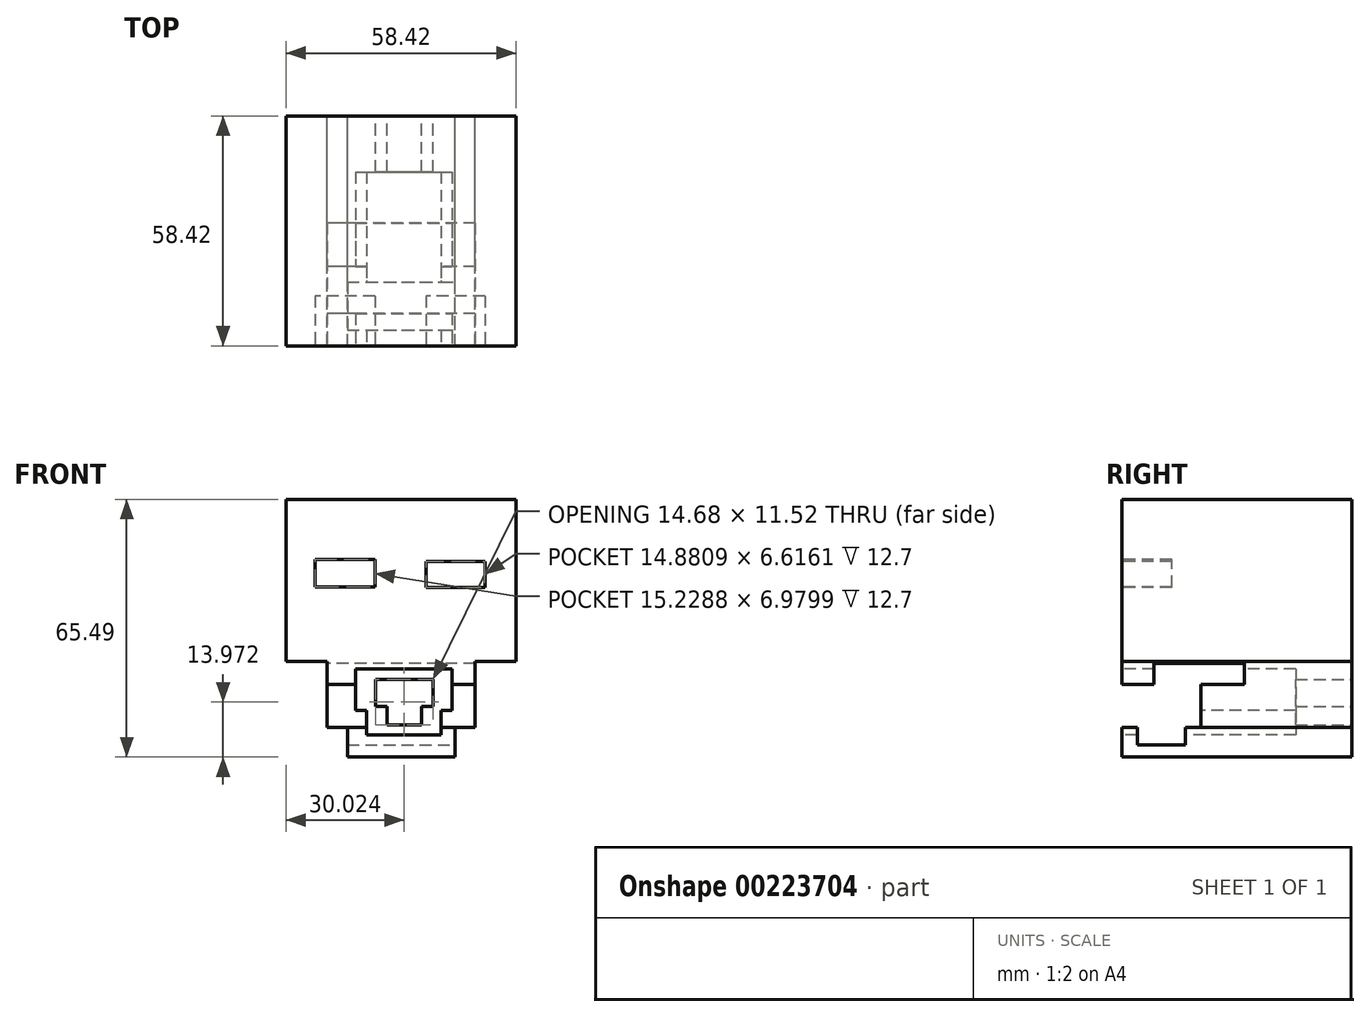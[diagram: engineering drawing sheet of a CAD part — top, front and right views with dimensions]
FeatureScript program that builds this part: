
annotation { "Feature Type Name" : "Feature", "Feature Type Description" : "" }
export const myFeature = defineFeature(function(context is Context, id is Id, definition is map)
    precondition{}
    {
        {
            var Q0;
            Q0=qCreatedBy(makeId("Front.planeOp"),FACE);
            var sketch = newSketch(context, id + "F0", { "sketchPlane" : qUnion([Q0])});
            skLineSegment(sketch, "E0.bottom", {"start": v(-29.2, 29.21) * mm, "end": v(29.21, 29.21) * mm});
            skLineSegment(sketch, "E0.left", {"start": v(-29.2, 29.21) * mm, "end": v(-29.21, -11.99) * mm});
            skLineSegment(sketch, "E0.right", {"start": v(29.21, 29.21) * mm, "end": v(29.2, -11.99) * mm});
            skPoint(sketch, "E0.middle", {"position": v(0, 0) * mm});
            skLineSegment(sketch, "E1", {"start": v(-29.21, -11.99) * mm, "end": v(-18.84, -11.99) * mm});
            skLineSegment(sketch, "E2", {"start": v(-18.84, -11.99) * mm, "end": v(-18.84, -28.7) * mm});
            skLineSegment(sketch, "E3.MirrorCS", {"start": v(18.84, -11.99) * mm, "end": v(18.84, -28.7) * mm});
            skLineSegment(sketch, "E4", {"start": v(-18.84, -28.7) * mm, "end": v(-13.65, -28.7) * mm});
            skLineSegment(sketch, "E5", {"start": v(18.84, -28.7) * mm, "end": v(13.74, -28.7) * mm});
            skLineSegment(sketch, "E6", {"start": v(-13.65, -28.7) * mm, "end": v(-13.65, -36.28) * mm});
            skLineSegment(sketch, "E7", {"start": v(13.74, -28.7) * mm, "end": v(13.74, -36.28) * mm});
            skLineSegment(sketch, "E8", {"start": v(-13.65, -36.28) * mm, "end": v(13.74, -36.28) * mm});
            skLineSegment(sketch, "E9.trimOffspring", {"start": v(18.84, -11.99) * mm, "end": v(29.2, -11.99) * mm});
            skSolve(sketch);
        }
        {
            var Q0;
            Q0 = qSketchRegion(id + "F0", true);
            extrude(context, id + "F1", {"entities" : qUnion([Q0]), "endBound" : BoundingType.SYMMETRIC, "depth" : 58.42 * mm});
        }
        {
            var Q0;
            Q0=makeQuery(id+"F1.opExtrude","CAP_FACE",FACE,{"disambiguationData":[OSD([sQuery(id+"F0.wireOp",EDGE,"E0.bottom"),sQuery(id+"F0.wireOp",EDGE,"E0.top"),sQuery(id+"F0.wireOp",EDGE,"E0.left"),sQuery(id+"F0.wireOp",EDGE,"E0.right")])],"isStart":false});
            var sketch = newSketch(context, id + "F2", { "sketchPlane" : qUnion([Q0])});
            skLineSegment(sketch, "E10.bottom", {"start": v(-6.65, 6.9) * mm, "end": v(-21.88, 6.9) * mm});
            skLineSegment(sketch, "E10.top", {"start": v(-6.65, 13.88) * mm, "end": v(-21.88, 13.88) * mm});
            skLineSegment(sketch, "E10.left", {"start": v(-6.65, 6.9) * mm, "end": v(-6.65, 13.88) * mm});
            skLineSegment(sketch, "E10.right", {"start": v(-21.88, 6.9) * mm, "end": v(-21.88, 13.88) * mm});
            skLineSegment(sketch, "E11.bottom", {"start": v(21.27, 6.85) * mm, "end": v(6.4, 6.85) * mm});
            skLineSegment(sketch, "E11.top", {"start": v(21.27, 13.46) * mm, "end": v(6.4, 13.46) * mm});
            skLineSegment(sketch, "E11.left", {"start": v(21.27, 6.85) * mm, "end": v(21.27, 13.46) * mm});
            skLineSegment(sketch, "E11.right", {"start": v(6.4, 6.85) * mm, "end": v(6.4, 13.46) * mm});
            skSolve(sketch);
        }
        {
            var Q0;
            Q0=makeQuery(id+"F2.imprint","IMPRINT",FACE,{"disambiguationData":[TD([[makeQuery(id+"F2.imprint","IMPRINT",EDGE,{"derivedFrom":sQuery(id+"F2.wireOp",EDGE,"89d0a196-2e3c-4021-a17d-25c8eb369dc5.bottom")}),-1.0]])]});
            var Q1;
            Q1=makeQuery(id+"F2.imprint","IMPRINT",FACE,{"disambiguationData":[TD([[makeQuery(id+"F2.imprint","IMPRINT",EDGE,{"derivedFrom":sQuery(id+"F2.wireOp",EDGE,"E10.bottom")}),-1.0]])]});
            var Q2;
            Q2=makeQuery(id+"F2.imprint","IMPRINT",FACE,{"disambiguationData":[TD([[makeQuery(id+"F2.imprint","IMPRINT",EDGE,{"derivedFrom":sQuery(id+"F2.wireOp",EDGE,"E11.bottom")}),-1.0]])]});
            extrude(context, id + "F3", {"entities" : qUnion([Q0, Q1, Q2]), "operationType" : NewBodyOperationType.REMOVE, "oppositeDirection" : true, "depth" : 12.7 * mm});
        }
        {
            var Q0;
            Q0=makeQuery(id+"F2.imprint","IMPRINT",FACE,{"disambiguationData":[TD([[makeQuery(id+"F2.imprint","IMPRINT",EDGE,{"derivedFrom":sQuery(id+"F2.wireOp",EDGE,"E10.bottom")}),1.0]])]});
            var sketch = newSketch(context, id + "F4", { "sketchPlane" : qUnion([Q0])});
            skLineSegment(sketch, "E12.top", {"start": v(-11.58, -24.48) * mm, "end": v(-8.78, -24.48) * mm});
            skLineSegment(sketch, "E12.left", {"start": v(-11.58, -13.84) * mm, "end": v(-11.58, -24.48) * mm});
            skLineSegment(sketch, "E12.right", {"start": v(12.97, -13.85) * mm, "end": v(12.97, -24.48) * mm});
            skLineSegment(sketch, "E13.top", {"start": v(-8.78, -30.6) * mm, "end": v(10.2, -30.6) * mm});
            skLineSegment(sketch, "E13.right", {"start": v(10.2, -24.48) * mm, "end": v(10.2, -30.6) * mm});
            skLineSegment(sketch, "E14.trimOffspring", {"start": v(10.2, -24.48) * mm, "end": v(12.97, -24.48) * mm});
            skLineSegment(sketch, "E15", {"start": v(-8.78, -24.48) * mm, "end": v(-8.78, -30.6) * mm});
            skLineSegment(sketch, "E16", {"start": v(-11.58, -13.84) * mm, "end": v(12.97, -13.85) * mm});
            skSolve(sketch);
        }
        {
            var Q0;
            Q0 = qSketchRegion(id + "F4", true);
            var Q1;
            Q1=makeQuery(id+"F1.opExtrude","CAP_FACE",FACE,{"disambiguationData":[OSD([sQuery(id+"F0.wireOp",EDGE,"E0.bottom"),sQuery(id+"F0.wireOp",EDGE,"E0.left"),sQuery(id+"F0.wireOp",EDGE,"E0.right"),sQuery(id+"F0.wireOp",EDGE,"E1"),sQuery(id+"F0.wireOp",EDGE,"E2"),sQuery(id+"F0.wireOp",EDGE,"E3.MirrorCS"),sQuery(id+"F0.wireOp",EDGE,"E4"),sQuery(id+"F0.wireOp",EDGE,"E5"),sQuery(id+"F0.wireOp",EDGE,"E6"),sQuery(id+"F0.wireOp",EDGE,"E7"),sQuery(id+"F0.wireOp",EDGE,"E8"),sQuery(id+"F0.wireOp",EDGE,"E9.trimOffspring")])],"isStart":true});
            extrude(context, id + "F5", {"entities" : qUnion([Q0]), "operationType" : NewBodyOperationType.REMOVE, "endBound" : BoundingType.UP_TO_SURFACE, "oppositeDirection" : true, "endBoundEntityFace" : qUnion([Q1]), "depth" : 25.4 * mm});
        }
        {
            var Q0;
            Q0=makeQuery(id+"F1.opExtrude","SWEPT_FACE",FACE,{"disambiguationData":[OSD([sQuery(id+"F0.wireOp",EDGE,"E2")])]});
            var sketch = newSketch(context, id + "F6", { "sketchPlane" : qUnion([Q0])});
            skLineSegment(sketch, "E17.bottom", {"start": v(-2, -12.45) * mm, "end": v(20.98, -12.45) * mm});
            skLineSegment(sketch, "E17.top", {"start": v(-2, -17.86) * mm, "end": v(9.04, -17.86) * mm});
            skLineSegment(sketch, "E17.left", {"start": v(-2, -12.45) * mm, "end": v(-2, -17.86) * mm});
            skLineSegment(sketch, "E17.right", {"start": v(20.98, -12.45) * mm, "end": v(20.98, -17.86) * mm});
            skLineSegment(sketch, "E18.bottom", {"start": v(20.98, -17.86) * mm, "end": v(29.31, -17.86) * mm});
            skLineSegment(sketch, "E18.top", {"start": v(9.04, -28.7) * mm, "end": v(29.31, -28.7) * mm});
            skLineSegment(sketch, "E18.left", {"start": v(9.04, -17.86) * mm, "end": v(9.04, -28.7) * mm});
            skLineSegment(sketch, "E18.right", {"start": v(29.31, -17.86) * mm, "end": v(29.31, -28.7) * mm});
            skSolve(sketch);
        }
        {
            var Q0;
            Q0 = qSketchRegion(id + "F6", true);
            var Q1;
            Q1=makeQuery(id+"F1.opExtrude","SWEPT_FACE",FACE,{"disambiguationData":[OSD([sQuery(id+"F0.wireOp",EDGE,"E3.MirrorCS")])]});
            extrude(context, id + "F7", {"entities" : qUnion([Q0]), "operationType" : NewBodyOperationType.REMOVE, "endBound" : BoundingType.UP_TO_SURFACE, "oppositeDirection" : true, "endBoundEntityFace" : qUnion([Q1]), "depth" : 25.4 * mm});
        }
        {
            var Q0;
            Q0=makeQuery(id+"F1.opExtrude","SWEPT_FACE",FACE,{"disambiguationData":[OSD([sQuery(id+"F0.wireOp",EDGE,"E7")])]});
            var sketch = newSketch(context, id + "F8", { "sketchPlane" : qUnion([Q0])});
            skLineSegment(sketch, "E19.bottom", {"start": v(-25.22, -33.19) * mm, "end": v(-13.05, -33.19) * mm});
            skLineSegment(sketch, "E19.top", {"start": v(-25.22, -28.7) * mm, "end": v(-13.05, -28.7) * mm});
            skLineSegment(sketch, "E19.left", {"start": v(-25.22, -33.19) * mm, "end": v(-25.22, -28.7) * mm});
            skLineSegment(sketch, "E19.right", {"start": v(-13.05, -33.19) * mm, "end": v(-13.05, -28.7) * mm});
            skSolve(sketch);
        }
        {
            var Q0;
            Q0 = qSketchRegion(id + "F8", true);
            var Q1;
            Q1=makeQuery(id+"F1.opExtrude","SWEPT_FACE",FACE,{"disambiguationData":[OSD([sQuery(id+"F0.wireOp",EDGE,"E6")])]});
            extrude(context, id + "F9", {"entities" : qUnion([Q0]), "operationType" : NewBodyOperationType.REMOVE, "endBound" : BoundingType.UP_TO_SURFACE, "oppositeDirection" : true, "endBoundEntityFace" : qUnion([Q1]), "depth" : 25.4 * mm});
        }
        {
            var Q0;
            Q0=makeQuery(id+"F1.opExtrude","CAP_FACE",FACE,{"disambiguationData":[OSD([sQuery(id+"F0.wireOp",EDGE,"E0.bottom"),sQuery(id+"F0.wireOp",EDGE,"E0.left"),sQuery(id+"F0.wireOp",EDGE,"E0.right"),sQuery(id+"F0.wireOp",EDGE,"E1"),sQuery(id+"F0.wireOp",EDGE,"E2"),sQuery(id+"F0.wireOp",EDGE,"E3.MirrorCS"),sQuery(id+"F0.wireOp",EDGE,"E4"),sQuery(id+"F0.wireOp",EDGE,"E5"),sQuery(id+"F0.wireOp",EDGE,"E6"),sQuery(id+"F0.wireOp",EDGE,"E7"),sQuery(id+"F0.wireOp",EDGE,"E8"),sQuery(id+"F0.wireOp",EDGE,"E9.trimOffspring")])],"isStart":true});
            var sketch = newSketch(context, id + "F10", { "sketchPlane" : qUnion([Q0])});
            skLineSegment(sketch, "E20.bottom", {"start": v(-15.34, -11.61) * mm, "end": v(12.82, -11.61) * mm});
            skLineSegment(sketch, "E20.top", {"start": v(-15.34, -26.3) * mm, "end": v(-12.97, -26.3) * mm});
            skLineSegment(sketch, "E20.left", {"start": v(-15.34, -11.61) * mm, "end": v(-15.34, -26.3) * mm});
            skLineSegment(sketch, "E20.right", {"start": v(12.82, -11.61) * mm, "end": v(12.82, -26.3) * mm});
            skLineSegment(sketch, "E21.trimOffspring", {"start": v(10.17, -26.3) * mm, "end": v(12.82, -26.3) * mm});
            skLineSegment(sketch, "E22", {"start": v(-12.97, -26.3) * mm, "end": v(-12.98, -31.88) * mm});
            skLineSegment(sketch, "E23", {"start": v(10.17, -26.3) * mm, "end": v(10.17, -31.88) * mm});
            skLineSegment(sketch, "E24", {"start": v(-12.98, -31.88) * mm, "end": v(10.17, -31.88) * mm});
            skSolve(sketch);
        }
        {
            var Q0;
            Q0 = qSketchRegion(id + "F10", true);
            extrude(context, id + "F11", {"entities" : qUnion([Q0]), "operationType" : NewBodyOperationType.ADD, "oppositeDirection" : true, "depth" : 14.22 * mm});
        }
        {
            var Q0;
            Q0=makeQuery(id+"F11.boolean.opBoolean","MERGE",FACE,{"derivedFrom":[makeQuery(id+"F1.opExtrude","CAP_FACE",FACE,{"disambiguationData":[OSD([sQuery(id+"F0.wireOp",EDGE,"E0.bottom"),sQuery(id+"F0.wireOp",EDGE,"E0.left"),sQuery(id+"F0.wireOp",EDGE,"E0.right"),sQuery(id+"F0.wireOp",EDGE,"E1"),sQuery(id+"F0.wireOp",EDGE,"E2"),sQuery(id+"F0.wireOp",EDGE,"E3.MirrorCS"),sQuery(id+"F0.wireOp",EDGE,"E4"),sQuery(id+"F0.wireOp",EDGE,"E5"),sQuery(id+"F0.wireOp",EDGE,"E6"),sQuery(id+"F0.wireOp",EDGE,"E7"),sQuery(id+"F0.wireOp",EDGE,"E8"),sQuery(id+"F0.wireOp",EDGE,"E9.trimOffspring")])],"isStart":true}),makeQuery(id+"F11.opExtrude","CAP_FACE",FACE,{"disambiguationData":[OSD([sQuery(id+"F10.wireOp",EDGE,"E20.bottom"),sQuery(id+"F10.wireOp",EDGE,"E20.top"),sQuery(id+"F10.wireOp",EDGE,"E20.left"),sQuery(id+"F10.wireOp",EDGE,"E20.right"),sQuery(id+"F10.wireOp",EDGE,"jttp3icE-9x9x-Tevf-4zcm-dXErHEorkXJk.bottom"),sQuery(id+"F10.wireOp",EDGE,"jttp3icE-9x9x-Tevf-4zcm-dXErHEorkXJk.left"),sQuery(id+"F10.wireOp",EDGE,"jttp3icE-9x9x-Tevf-4zcm-dXErHEorkXJk.right"),sQuery(id+"F10.wireOp",EDGE,"E21.trimOffspring")])],"isStart":true})]});
            var sketch = newSketch(context, id + "F12", { "sketchPlane" : qUnion([Q0])});
            skLineSegment(sketch, "E25.bottom", {"start": v(6.53, -16.55) * mm, "end": v(-8.15, -16.55) * mm});
            skLineSegment(sketch, "E25.top", {"start": v(6.53, -23.45) * mm, "end": v(3.52, -23.45) * mm});
            skLineSegment(sketch, "E25.left", {"start": v(6.53, -16.55) * mm, "end": v(6.53, -23.45) * mm});
            skLineSegment(sketch, "E25.right", {"start": v(-8.15, -16.55) * mm, "end": v(-8.15, -23.45) * mm});
            skLineSegment(sketch, "E26.top", {"start": v(3.52, -28.07) * mm, "end": v(-5.14, -28.07) * mm});
            skLineSegment(sketch, "E26.left", {"start": v(3.52, -23.45) * mm, "end": v(3.52, -28.07) * mm});
            skLineSegment(sketch, "E26.right", {"start": v(-5.14, -23.45) * mm, "end": v(-5.14, -28.07) * mm});
            skLineSegment(sketch, "E27.trimOffspring", {"start": v(-5.14, -23.45) * mm, "end": v(-8.15, -23.45) * mm});
            skSolve(sketch);
        }
        {
            var Q0;
            Q0 = qSketchRegion(id + "F12", true);
            var Q1;
            Q1=makeQuery(id+"F11.opExtrude","CAP_FACE",FACE,{"disambiguationData":[OSD([sQuery(id+"F10.wireOp",EDGE,"E20.bottom"),sQuery(id+"F10.wireOp",EDGE,"E20.top"),sQuery(id+"F10.wireOp",EDGE,"E20.left"),sQuery(id+"F10.wireOp",EDGE,"E20.right"),sQuery(id+"F10.wireOp",EDGE,"jttp3icE-9x9x-Tevf-4zcm-dXErHEorkXJk.bottom"),sQuery(id+"F10.wireOp",EDGE,"jttp3icE-9x9x-Tevf-4zcm-dXErHEorkXJk.left"),sQuery(id+"F10.wireOp",EDGE,"jttp3icE-9x9x-Tevf-4zcm-dXErHEorkXJk.right"),sQuery(id+"F10.wireOp",EDGE,"E21.trimOffspring")])],"isStart":false});
            extrude(context, id + "F13", {"entities" : qUnion([Q0]), "operationType" : NewBodyOperationType.REMOVE, "endBound" : BoundingType.UP_TO_SURFACE, "oppositeDirection" : true, "endBoundEntityFace" : qUnion([Q1]), "depth" : 25.4 * mm});
        }
    });
